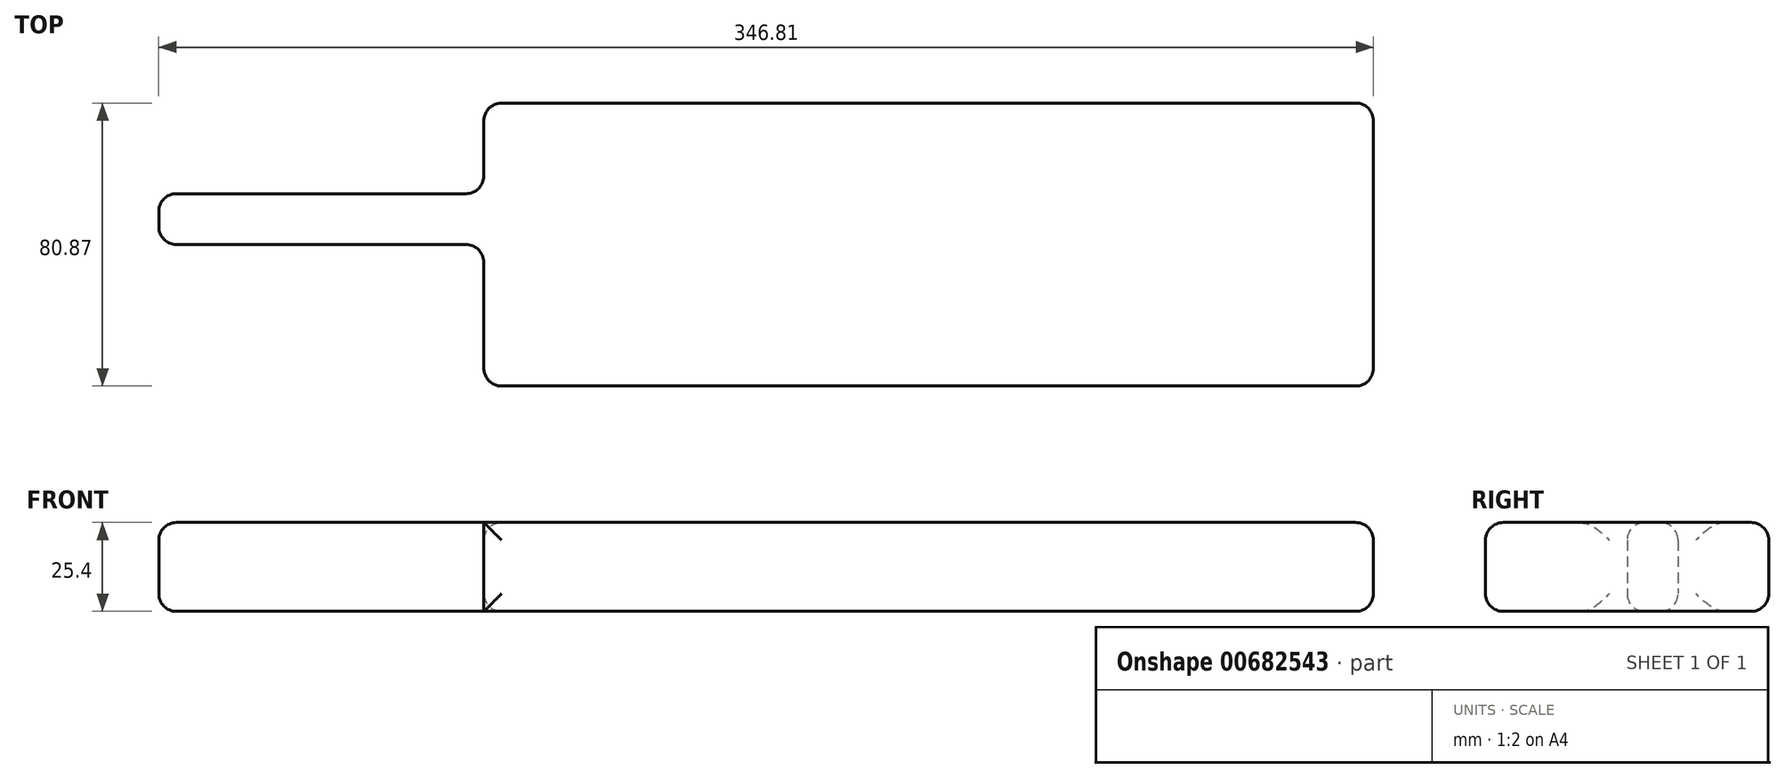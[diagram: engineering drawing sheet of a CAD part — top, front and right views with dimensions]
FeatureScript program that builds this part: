
annotation { "Feature Type Name" : "Feature", "Feature Type Description" : "" }
export const myFeature = defineFeature(function(context is Context, id is Id, definition is map)
    precondition{}
    {
        {
            var Q0;
            Q0=qCreatedBy(makeId("Top.planeOp"),FACE);
            var sketch = newSketch(context, id + "F0", { "sketchPlane" : qUnion([Q0])});
            skLineSegment(sketch, "E0.bottom", {"start": v(1.8, 0) * mm, "end": v(0, 0) * mm});
            skLineSegment(sketch, "E0.top", {"start": v(1.8, 0) * mm, "end": v(0, 0) * mm});
            skLineSegment(sketch, "E0.left", {"start": v(1.8, 0) * mm, "end": v(1.8, 0) * mm});
            skLineSegment(sketch, "E0.right", {"start": v(0, 0) * mm, "end": v(0, 0) * mm});
            skLineSegment(sketch, "E1.bottom", {"start": v(0, 0) * mm, "end": v(254, 0) * mm});
            skLineSegment(sketch, "E1.top", {"start": v(0, 80.87) * mm, "end": v(254, 80.87) * mm});
            skLineSegment(sketch, "E1.left", {"start": v(0, 0) * mm, "end": v(0, 80.87) * mm});
            skLineSegment(sketch, "E1.right", {"start": v(254, 0) * mm, "end": v(254, 80.87) * mm});
            skPoint(sketch, "E2.oppositeSnap0", {"position": v(0, 40.43) * mm});
            skLineSegment(sketch, "E2.bottom", {"start": v(0, 54.97) * mm, "end": v(-92.8, 54.97) * mm});
            skLineSegment(sketch, "E2.top", {"start": v(0, 40.43) * mm, "end": v(-92.8, 40.43) * mm});
            skLineSegment(sketch, "E2.left", {"start": v(0, 54.97) * mm, "end": v(0, 40.43) * mm});
            skLineSegment(sketch, "E2.right", {"start": v(-92.8, 54.97) * mm, "end": v(-92.8, 40.43) * mm});
            skSolve(sketch);
        }
        {
            var Q0;
            Q0=makeQuery(id+"F0.imprint","IMPRINT",FACE,{"disambiguationData":[TD([[makeQuery(id+"F0.imprint","IMPRINT",EDGE,{"derivedFrom":sQuery(id+"F0.wireOp",EDGE,"E2.bottom")}),1.0]])]});
            var Q1;
            {var subQ1=sQuery(id+"F0.wireOp",EDGE,"E1.top");Q1=makeQuery(id+"F0.imprint","IMPRINT",FACE,{"disambiguationData":[TD([[makeQuery(id+"F0.imprint","IMPRINT",EDGE,{"derivedFrom":subQ1}),-1.0]])]});}
            extrude(context, id + "F1", {"entities" : qUnion([Q0, Q1]), "depth" : 25.4 * mm, "offsetDistance" : 25.4 * mm});
        }
        {
            var Q0;
            Q0=makeQuery(id+"F1.opExtrude","SWEPT_FACE",FACE,{"disambiguationData":[OSD([sQuery(id+"F0.wireOp",EDGE,"E1.bottom")])]});
            fillet(context, id + "F2", {"entities" : qUnion([Q0]), "radius" : 5.08 * mm, "tangentPropagation" : true, "allowEdgeOverflow" : false});
        }
        {
            var Q0;
            Q0=makeQuery(id+"F1.opExtrude","CAP_EDGE",EDGE,{"disambiguationData":[OSD([sQuery(id+"F0.wireOp",EDGE,"E1.right")])],"isStart":false});
            var Q1;
            Q1=makeQuery(id+"F1.opExtrude","SWEPT_FACE",FACE,{"disambiguationData":[OSD([sQuery(id+"F0.wireOp",EDGE,"E1.right")])]});
            fillet(context, id + "F3", {"entities" : qUnion([Q0, Q1]), "radius" : 5.08 * mm, "tangentPropagation" : true, "allowEdgeOverflow" : false});
        }
        {
            var Q0;
            Q0=makeQuery(id+"F1.opExtrude","SWEPT_FACE",FACE,{"disambiguationData":[OSD([sQuery(id+"F0.wireOp",EDGE,"E1.top")])]});
            fillet(context, id + "F4", {"entities" : qUnion([Q0]), "radius" : 5.08 * mm, "tangentPropagation" : true, "allowEdgeOverflow" : false});
        }
        {
            var Q0;
            Q0=makeQuery(id+"F1.opExtrude","SWEPT_FACE",FACE,{"disambiguationData":[OSD([sQuery(id+"F0.wireOp",EDGE,"E2.bottom")])]});
            fillet(context, id + "F5", {"entities" : qUnion([Q0]), "radius" : 5.08 * mm, "tangentPropagation" : true, "allowEdgeOverflow" : false});
        }
        {
            var Q0;
            Q0=makeQuery(id+"F1.opExtrude","SWEPT_FACE",FACE,{"disambiguationData":[OSD([sQuery(id+"F0.wireOp",EDGE,"E2.right")])]});
            fillet(context, id + "F6", {"entities" : qUnion([Q0]), "radius" : 5.08 * mm, "tangentPropagation" : true, "allowEdgeOverflow" : false});
        }
        {
            var Q0;
            Q0=makeQuery(id+"F1.opExtrude","SWEPT_FACE",FACE,{"disambiguationData":[OSD([sQuery(id+"F0.wireOp",EDGE,"E2.top")])]});
            fillet(context, id + "F7", {"entities" : qUnion([Q0]), "radius" : 5.08 * mm, "tangentPropagation" : true, "allowEdgeOverflow" : false});
        }
    });
